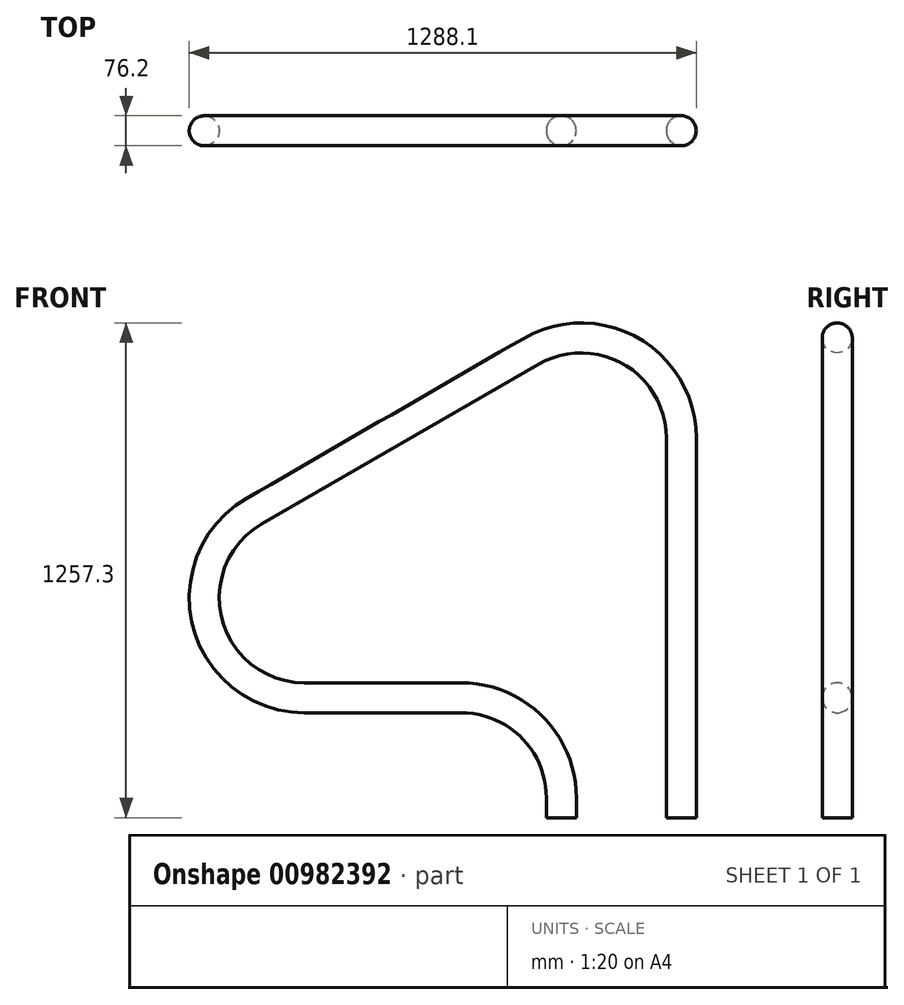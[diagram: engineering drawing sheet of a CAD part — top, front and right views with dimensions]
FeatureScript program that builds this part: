
annotation { "Feature Type Name" : "Feature", "Feature Type Description" : "" }
export const myFeature = defineFeature(function(context is Context, id is Id, definition is map)
    precondition{}
    {
        {
            var Q0;
            Q0=qCreatedBy(makeId("Front.planeOp"),FACE);
            var sketch = newSketch(context, id + "F0", { "sketchPlane" : qUnion([Q0])});
            skLineSegment(sketch, "E0", {"start": v(-464.53, 0) * mm, "end": v(-464.53, 965.2) * mm});
            skLineSegment(sketch, "E1", {"start": v(-845.53, 1185.17) * mm, "end": v(-1549.43, 778.77) * mm});
            skLineSegment(sketch, "E2", {"start": v(-1422.43, 304.8) * mm, "end": v(-1023.33, 304.8) * mm});
            skLineSegment(sketch, "E3", {"start": v(-769.33, 50.8) * mm, "end": v(-769.33, 0) * mm});
            skPoint(sketch, "E4.visualSharp", {"position": v(-464.53, 1405.14) * mm});
            skArc(sketch, "E4.filletArc", {"start": v(-464.54, 1393.75) * mm, "mid": v(-464.54, 1393.82) * mm, "end": v(-464.53, 1393.89) * mm});
            skArc(sketch, "E5.filletArc", {"start": v(-464.53, 965.2) * mm, "mid": v(-591.53, 1185.17) * mm, "end": v(-845.53, 1185.17) * mm});
            skPoint(sketch, "E6.visualSharp", {"position": v(-2370.37, 304.8) * mm});
            skArc(sketch, "E6.filletArc", {"start": v(-1549.43, 778.77) * mm, "mid": v(-1667.78, 493.06) * mm, "end": v(-1422.43, 304.8) * mm});
            skPoint(sketch, "E7.visualSharp", {"position": v(-769.33, 304.8) * mm});
            skArc(sketch, "E7.filletArc", {"start": v(-769.33, 50.8) * mm, "mid": v(-843.72, 230.4) * mm, "end": v(-1023.33, 304.8) * mm});
            skLineSegment(sketch, "E8", {"start": v(-1092.32, 1219.2) * mm, "end": v(-290.95, 1219.2) * mm, "construction": true});
            skSolve(sketch);
        }
        {
            var Q0;
            Q0=sQuery(id+"F0.wireOp",VERTEX,"E0.start");
            var Q1;
            Q1=sQuery(id+"F0.wireOp",EDGE,"E0");
            cPlane(context, id + "F1", {"entities" : qUnion([Q0, Q1]), "cplaneType" : CPlaneType.LINE_POINT, "offset" : 25.4 * mm, "width" : 152.4 * mm, "height" : 152.4 * mm});
        }
        {
            var Q0;
            Q0=qCreatedBy(id+"F1.planeOp",FACE);
            var sketch = newSketch(context, id + "F2", { "sketchPlane" : qUnion([Q0])});
            skCircle(sketch, "E9", {"center": v(-464.53, 0) * mm, "radius": 38.1 * mm});
            skSolve(sketch);
        }
        {
            var Q0;
            Q0=makeQuery(id+"F2.imprint","IMPRINT",FACE,{"disambiguationData":[TD([[makeQuery(id+"F2.imprint","IMPRINT",EDGE,{"derivedFrom":sQuery(id+"F2.wireOp",EDGE,"E9")}),1.0]])]});
            var Q1;
            Q1=sQuery(id+"F0.wireOp",EDGE,"E0");
            var Q2;
            Q2=sQuery(id+"F0.wireOp",EDGE,"E5.filletArc");
            var Q3;
            Q3=sQuery(id+"F0.wireOp",EDGE,"E1");
            var Q4;
            Q4=sQuery(id+"F0.wireOp",EDGE,"E6.filletArc");
            var Q5;
            Q5=sQuery(id+"F0.wireOp",EDGE,"E2");
            var Q6;
            Q6=sQuery(id+"F0.wireOp",EDGE,"E7.filletArc");
            var Q7;
            Q7=sQuery(id+"F0.wireOp",EDGE,"E3");
            sweep(context, id + "F3", {"profiles" : qUnion([Q0]), "path" : qUnion([Q1, Q2, Q3, Q4, Q5, Q6, Q7])});
        }
    });
